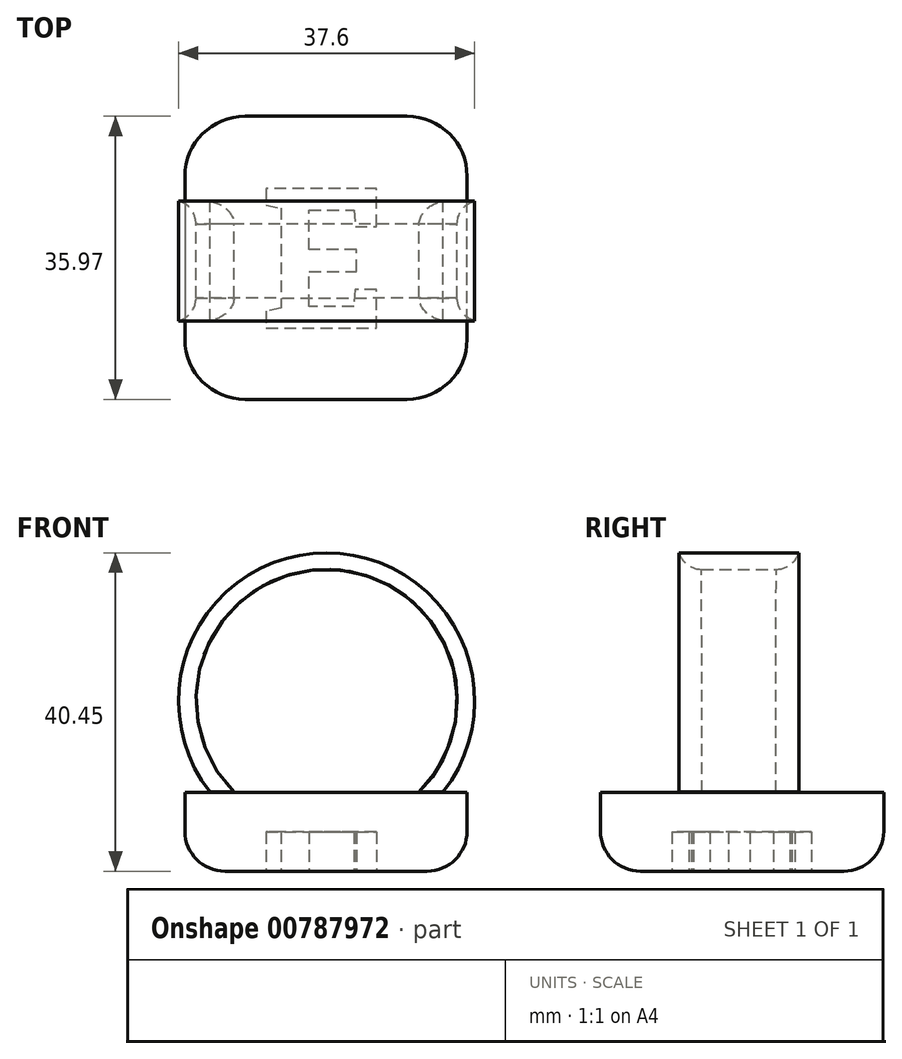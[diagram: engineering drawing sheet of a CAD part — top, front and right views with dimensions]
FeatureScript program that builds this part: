
annotation { "Feature Type Name" : "Feature", "Feature Type Description" : "" }
export const myFeature = defineFeature(function(context is Context, id is Id, definition is map)
    precondition{}
    {
        {
            var Q0;
            Q0=qCreatedBy(makeId("Top.planeOp"),FACE);
            var sketch = newSketch(context, id + "F0", { "sketchPlane" : qUnion([Q0])});
            skLineSegment(sketch, "E0", {"start": v(-35.83, -25.18) * mm, "end": v(0, -25.18) * mm});
            skLineSegment(sketch, "E1", {"start": v(0, -25.18) * mm, "end": v(0, 10.8) * mm});
            skLineSegment(sketch, "E2", {"start": v(0, 10.8) * mm, "end": v(-35.83, 10.8) * mm});
            skLineSegment(sketch, "E3", {"start": v(-35.83, 10.8) * mm, "end": v(-35.83, -25.18) * mm});
            skSolve(sketch);
        }
        {
            var Q0;
            Q0=qSketchRegion(id+"F0",true);
            extrude(context, id + "F1", {"entities" : qUnion([Q0]), "depth" : 10 * mm, "offsetDistance" : 25.4 * mm});
        }
        {
            var Q0;
            Q0=qCreatedBy(makeId("Front.planeOp"),FACE);
            var sketch = newSketch(context, id + "F2", { "sketchPlane" : qUnion([Q0])});
            skLineSegment(sketch, "E4", {"start": v(-32.65, 10.06) * mm, "end": v(-29.6, 10.06) * mm});
            skLineSegment(sketch, "E5", {"start": v(-3.05, 10.06) * mm, "end": v(-6.1, 10.06) * mm});
            skArc(sketch, "E6", {"start": v(-6.1, 10.06) * mm, "mid": v(-17.85, 38.36) * mm, "end": v(-29.6, 10.06) * mm});
            skArc(sketch, "E7", {"start": v(-3.05, 10.06) * mm, "mid": v(-17.85, 40.45) * mm, "end": v(-32.65, 10.06) * mm});
            skPoint(sketch, "E8.orphan", {"position": v(-35.7, 10.06) * mm});
            skPoint(sketch, "E9.orphan", {"position": v(0, 10.06) * mm});
            skSolve(sketch);
        }
        {
            var Q0;
            Q0=makeQuery(id+"F1.opExtrude","SWEPT_EDGE",EDGE,{"disambiguationData":[OSD([sQuery(id+"F0.wireOp",EDGE,"E0"),sQuery(id+"F0.wireOp",EDGE,"E3")])]});
            var Q1;
            Q1=makeQuery(id+"F1.opExtrude","SWEPT_EDGE",EDGE,{"disambiguationData":[OSD([sQuery(id+"F0.wireOp",EDGE,"E2"),sQuery(id+"F0.wireOp",EDGE,"E3")])]});
            var Q2;
            Q2=makeQuery(id+"F1.opExtrude","SWEPT_EDGE",EDGE,{"disambiguationData":[OSD([sQuery(id+"F0.wireOp",EDGE,"E1"),sQuery(id+"F0.wireOp",EDGE,"E2")])]});
            var Q3;
            Q3=makeQuery(id+"F1.opExtrude","SWEPT_EDGE",EDGE,{"disambiguationData":[OSD([sQuery(id+"F0.wireOp",EDGE,"E0"),sQuery(id+"F0.wireOp",EDGE,"E1")])]});
            fillet(context, id + "F3", {"entities" : qUnion([Q0, Q1, Q2, Q3]), "radius" : 7.62 * mm, "tangentPropagation" : true, "allowEdgeOverflow" : false});
        }
        {
            var Q0;
            Q0=makeQuery(id+"F1.opExtrude","CAP_EDGE",EDGE,{"disambiguationData":[OSD([sQuery(id+"F0.wireOp",EDGE,"E0")])],"isStart":true});
            var Q1;
            Q1=makeQuery(id+"F1.opExtrude","CAP_EDGE",EDGE,{"disambiguationData":[OSD([sQuery(id+"F0.wireOp",EDGE,"E3")])],"isStart":true});
            var Q2;
            {var subQ0=sQuery(id+"F0.wireOp",EDGE,"E3");var subQ1=sQuery(id+"F0.wireOp",EDGE,"E0");Q2=makeQuery(id+"F3.opFillet","BLEND_EDGE",EDGE,{"blendedFrom":[makeQuery(id+"F1.opExtrude","SWEPT_EDGE",EDGE,{"disambiguationData":[OSD([subQ1,subQ0])]}),makeQuery(id+"F1.opExtrude","CAP_FACE",FACE,{"disambiguationData":[OSD([subQ1,sQuery(id+"F0.wireOp",EDGE,"E1"),sQuery(id+"F0.wireOp",EDGE,"E2"),subQ0])],"isStart":true})],"blendedInto":[makeQuery(id+"F1.opExtrude","CAP_FACE",FACE,{"disambiguationData":[OSD([subQ1,sQuery(id+"F0.wireOp",EDGE,"E1"),sQuery(id+"F0.wireOp",EDGE,"E2"),subQ0])],"isStart":true})]});}
            var Q3;
            {var subQ0=sQuery(id+"F0.wireOp",EDGE,"E1");var subQ1=sQuery(id+"F0.wireOp",EDGE,"E0");Q3=makeQuery(id+"F3.opFillet","BLEND_EDGE",EDGE,{"blendedFrom":[makeQuery(id+"F1.opExtrude","SWEPT_EDGE",EDGE,{"disambiguationData":[OSD([subQ1,subQ0])]}),makeQuery(id+"F1.opExtrude","CAP_FACE",FACE,{"disambiguationData":[OSD([subQ1,subQ0,sQuery(id+"F0.wireOp",EDGE,"E2"),sQuery(id+"F0.wireOp",EDGE,"E3")])],"isStart":true})],"blendedInto":[makeQuery(id+"F1.opExtrude","CAP_FACE",FACE,{"disambiguationData":[OSD([subQ1,subQ0,sQuery(id+"F0.wireOp",EDGE,"E2"),sQuery(id+"F0.wireOp",EDGE,"E3")])],"isStart":true})]});}
            var Q4;
            Q4=makeQuery(id+"F1.opExtrude","CAP_EDGE",EDGE,{"disambiguationData":[OSD([sQuery(id+"F0.wireOp",EDGE,"E1")])],"isStart":true});
            var Q5;
            {var subQ0=sQuery(id+"F0.wireOp",EDGE,"E2");var subQ1=sQuery(id+"F0.wireOp",EDGE,"E1");Q5=makeQuery(id+"F3.opFillet","BLEND_EDGE",EDGE,{"blendedFrom":[makeQuery(id+"F1.opExtrude","SWEPT_EDGE",EDGE,{"disambiguationData":[OSD([subQ1,subQ0])]}),makeQuery(id+"F1.opExtrude","CAP_FACE",FACE,{"disambiguationData":[OSD([sQuery(id+"F0.wireOp",EDGE,"E0"),subQ1,subQ0,sQuery(id+"F0.wireOp",EDGE,"E3")])],"isStart":true})],"blendedInto":[makeQuery(id+"F1.opExtrude","CAP_FACE",FACE,{"disambiguationData":[OSD([sQuery(id+"F0.wireOp",EDGE,"E0"),subQ1,subQ0,sQuery(id+"F0.wireOp",EDGE,"E3")])],"isStart":true})]});}
            var Q6;
            Q6=makeQuery(id+"F1.opExtrude","CAP_EDGE",EDGE,{"disambiguationData":[OSD([sQuery(id+"F0.wireOp",EDGE,"E2")])],"isStart":true});
            var Q7;
            {var subQ0=sQuery(id+"F0.wireOp",EDGE,"E3");var subQ1=sQuery(id+"F0.wireOp",EDGE,"E2");Q7=makeQuery(id+"F3.opFillet","BLEND_EDGE",EDGE,{"blendedFrom":[makeQuery(id+"F1.opExtrude","SWEPT_EDGE",EDGE,{"disambiguationData":[OSD([subQ1,subQ0])]}),makeQuery(id+"F1.opExtrude","CAP_FACE",FACE,{"disambiguationData":[OSD([sQuery(id+"F0.wireOp",EDGE,"E0"),sQuery(id+"F0.wireOp",EDGE,"E1"),subQ1,subQ0])],"isStart":true})],"blendedInto":[makeQuery(id+"F1.opExtrude","CAP_FACE",FACE,{"disambiguationData":[OSD([sQuery(id+"F0.wireOp",EDGE,"E0"),sQuery(id+"F0.wireOp",EDGE,"E1"),subQ1,subQ0])],"isStart":true})]});}
            fillet(context, id + "F4", {"entities" : qUnion([Q0, Q1, Q2, Q3, Q4, Q5, Q6, Q7]), "radius" : 5.08 * mm, "tangentPropagation" : true, "allowEdgeOverflow" : false});
        }
        {
            var Q0;
            Q0=makeQuery(id+"F1.opExtrude","CAP_FACE",FACE,{"disambiguationData":[OSD([sQuery(id+"F0.wireOp",EDGE,"E0"),sQuery(id+"F0.wireOp",EDGE,"E1"),sQuery(id+"F0.wireOp",EDGE,"E2"),sQuery(id+"F0.wireOp",EDGE,"E3")])],"isStart":true});
            var sketch = newSketch(context, id + "F5", { "sketchPlane" : qUnion([Q0])});
            skSolve(sketch);
        }
        {
            var Q0;
            {var subQ0=sQuery(id+"F0.wireOp",EDGE,"E3");var subQ1=sQuery(id+"F0.wireOp",EDGE,"E2");var subQ2=sQuery(id+"F0.wireOp",EDGE,"E1");var subQ3=sQuery(id+"F0.wireOp",EDGE,"E0");var subQ4=makeQuery(id+"F1.opExtrude","CAP_FACE",FACE,{"disambiguationData":[OSD([subQ3,subQ2,subQ1,subQ0])],"isStart":true});var subQ5=subQ4;Q0=makeQuery(id+"F5.imprint","IMPRINT",FACE,{"disambiguationData":[TD([[makeQuery(id+"F5.imprint","IMPRINT",EDGE,{"derivedFrom":makeQuery(id+"F4.opFillet","BLEND_EDGE",EDGE,{"blendedFrom":[makeQuery(id+"F1.opExtrude","CAP_EDGE",EDGE,{"disambiguationData":[OSD([subQ3])],"isStart":true}),subQ5],"blendedInto":[subQ5]})}),1.0]])]});}
            var sketch = newSketch(context, id + "F6", { "sketchPlane" : qUnion([Q0])});
            skText(sketch, "E10", { "text": "E", "fontName": "RobotoSlab-Bold.ttf"});
            const initialGuessF6  = {"E10": [-0.0262, -0.00163, 1, 0, 0.01797]};
            skSetInitialGuess(sketch, initialGuessF6);
            skSolve(sketch);
        }
        {
            var Q0;
            Q0=qSketchRegion(id+"F6",true);
            extrude(context, id + "F7", {"entities" : qUnion([Q0]), "operationType" : NewBodyOperationType.REMOVE, "oppositeDirection" : true, "depth" : 5 * mm, "offsetDistance" : 25.4 * mm});
        }
        {
            var Q0;
            Q0=qSketchRegion(id+"F2",true);
            extrude(context, id + "F8", {"entities" : qUnion([Q0]), "depth" : 15.2 * mm, "offsetDistance" : 25 * mm});
        }
        {
            var Q0;
            Q0=makeQuery(id+"F8.opExtrude","CAP_EDGE",EDGE,{"disambiguationData":[OSD([sQuery(id+"F2.wireOp",EDGE,"E6")])],"isStart":false});
            fillet(context, id + "F9", {"entities" : qUnion([Q0]), "radius" : 3 * mm, "tangentPropagation" : true, "allowEdgeOverflow" : false});
        }
        {
            var Q0;
            Q0=makeQuery(id+"F8.opExtrude","CAP_EDGE",EDGE,{"disambiguationData":[OSD([sQuery(id+"F2.wireOp",EDGE,"E6")])],"isStart":true});
            fillet(context, id + "F10", {"entities" : qUnion([Q0]), "radius" : 3 * mm, "tangentPropagation" : true, "allowEdgeOverflow" : false});
        }
    });
